# Revit family: Round Mirror 800mm_RFA
name_source: partatom
category: Generic Models
units: mm (PartAtom-declared; Revit-internal decimal feet)

## family parameters
Always vertical = Yes
Can host rebar = No
Cut with Voids When Loaded = No
Maintain Annotation Orientation = No
OmniClass Number = 23.40.95.17.17
OmniClass Title = Mirrors
Part Type = Normal
Room Calculation Point = No
Round Connector Dimension = Use Diameter
Shared = No
Work Plane-Based = No

## types (1)
- Standard
    Category = Mirrors
    Default Elevation = 0 mm  [stored 0 ft]
    Installation Guide = https://cdn.bfldr.com
    Part Number = 15846 (Brass), 15847 (Copper), 15848 (Gunmetal), 15849 (Black), 15850 (Stainless Steel)
    QR Link = https://abi.guide
    Spec Image = https://cdn.bfldr.com
    Title = Round Mirror 800mm

note: [stored X ft] marks values corroborated as IEEE doubles in the binary element streams (Revit-internal decimal feet)

## geometry (parser evidence)
native form markers: Sweep x3
no freeform markers — native parametric forms only
